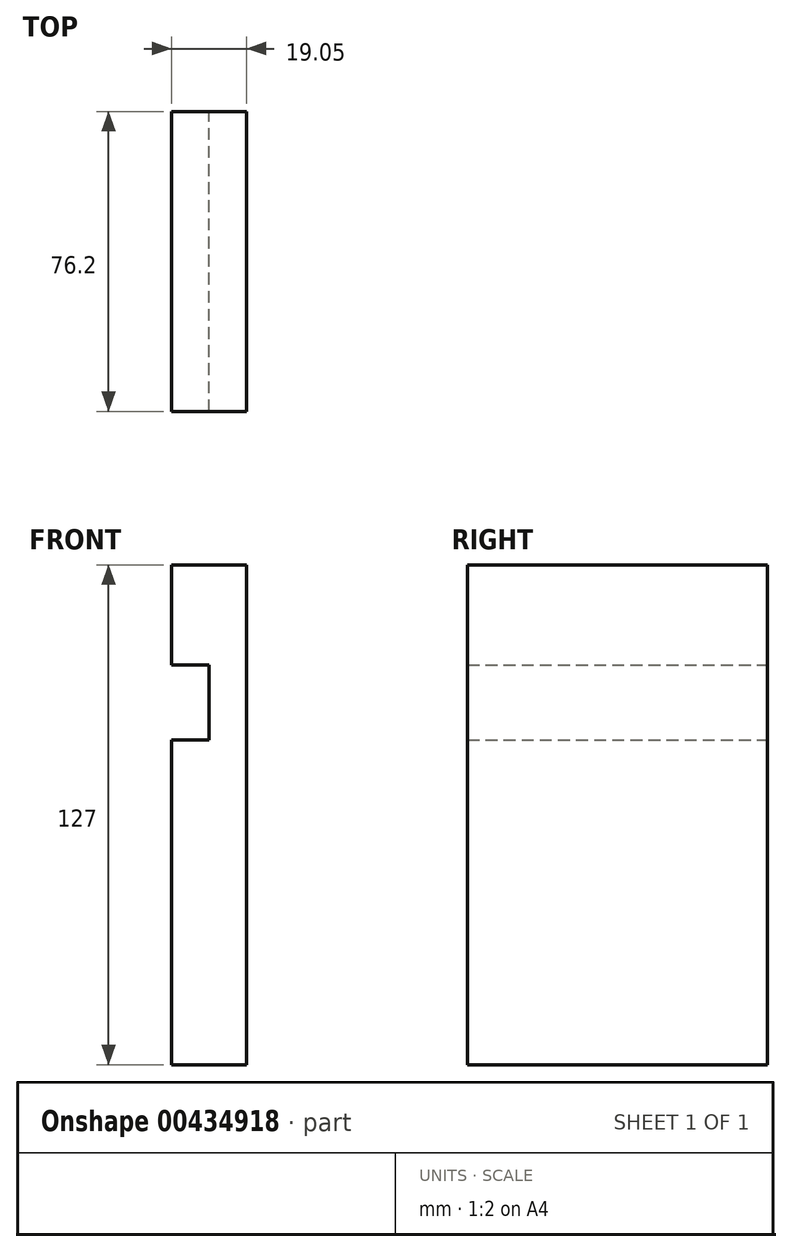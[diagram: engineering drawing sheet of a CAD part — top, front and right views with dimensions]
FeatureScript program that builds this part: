
annotation { "Feature Type Name" : "Feature", "Feature Type Description" : "" }
export const myFeature = defineFeature(function(context is Context, id is Id, definition is map)
    precondition{}
    {
        {
            var Q0;
            Q0=qCreatedBy(makeId("Front.planeOp"),FACE);
            var sketch = newSketch(context, id + "F0", { "sketchPlane" : qUnion([Q0])});
            skLineSegment(sketch, "E0", {"start": v(0, 0) * mm, "end": v(-19.05, 0) * mm});
            skLineSegment(sketch, "E1", {"start": v(0, 0) * mm, "end": v(0, 127) * mm});
            skLineSegment(sketch, "E2", {"start": v(0, 127) * mm, "end": v(-19.05, 127) * mm});
            skLineSegment(sketch, "E3", {"start": v(-19.05, 127) * mm, "end": v(-19.05, 101.6) * mm});
            skLineSegment(sketch, "E4", {"start": v(-19.05, 101.6) * mm, "end": v(-9.52, 101.6) * mm});
            skLineSegment(sketch, "E5", {"start": v(-9.52, 101.6) * mm, "end": v(-9.52, 82.55) * mm});
            skLineSegment(sketch, "E6", {"start": v(-9.52, 82.55) * mm, "end": v(-19.05, 82.55) * mm});
            skLineSegment(sketch, "E7", {"start": v(-19.05, 82.55) * mm, "end": v(-19.05, 0) * mm});
            skSolve(sketch);
        }
        {
            var Q0;
            Q0=qSketchRegion(id+"F0",true);
            extrude(context, id + "F1", {"entities" : qUnion([Q0]), "depth" : 76.2 * mm});
        }
    });
